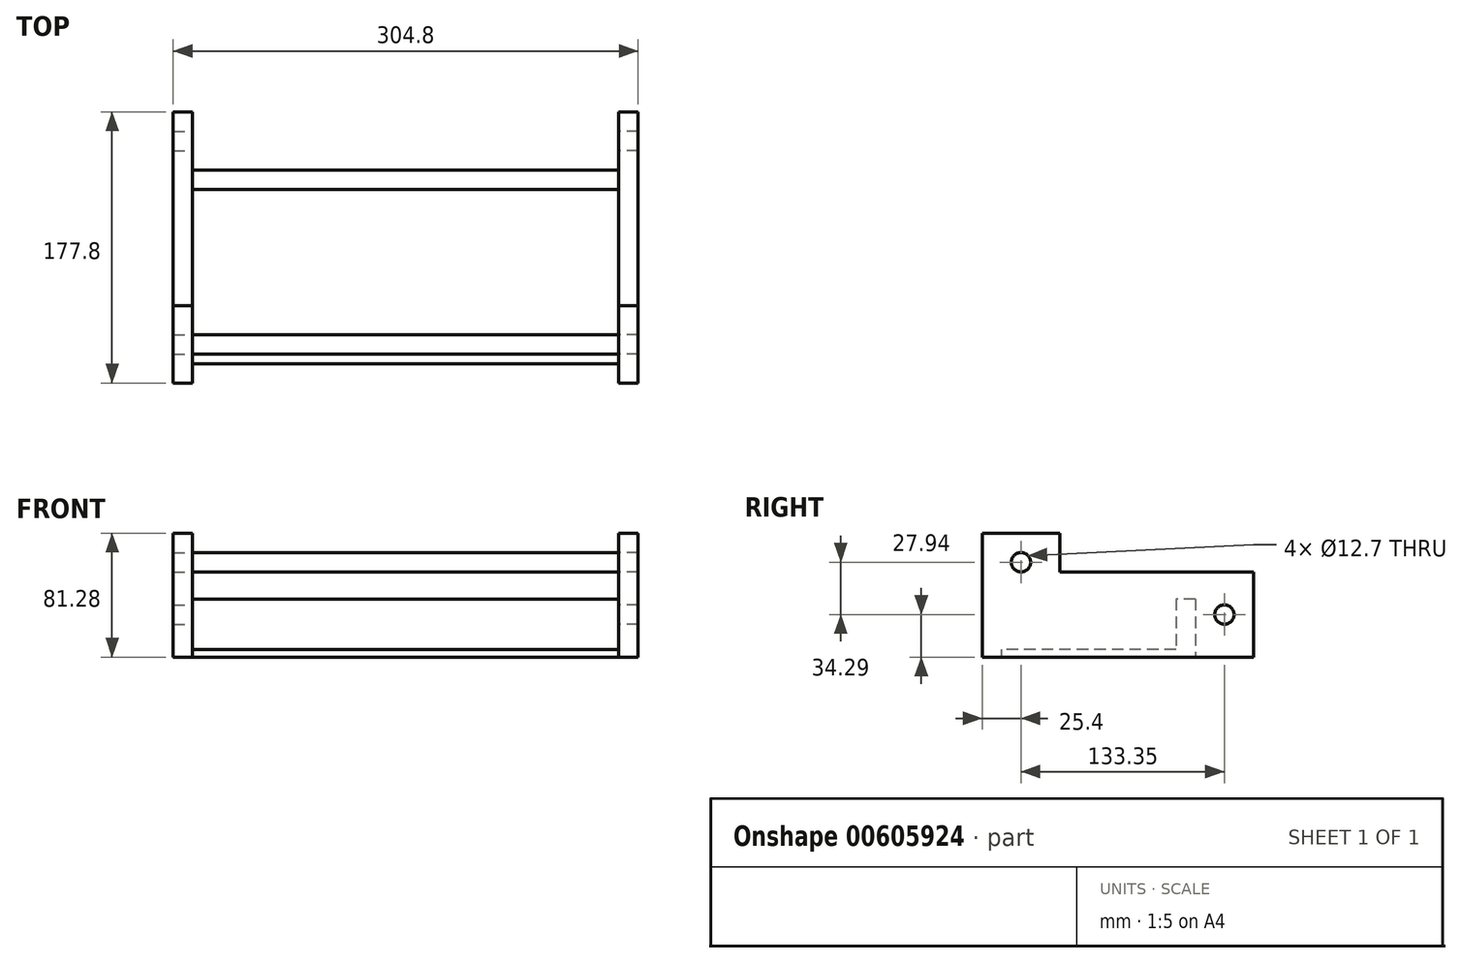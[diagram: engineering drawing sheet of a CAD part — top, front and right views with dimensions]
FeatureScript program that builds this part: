
annotation { "Feature Type Name" : "Feature", "Feature Type Description" : "" }
export const myFeature = defineFeature(function(context is Context, id is Id, definition is map)
    precondition{}
    {
        {
            var Q0;
            Q0=qCreatedBy(makeId("Top.planeOp"),FACE);
            var sketch = newSketch(context, id + "F0", { "sketchPlane" : qUnion([Q0])});
            skLineSegment(sketch, "E0.bottom", {"start": v(139.7, 63.5) * mm, "end": v(-139.7, 63.5) * mm});
            skLineSegment(sketch, "E0.top", {"start": v(139.7, -63.5) * mm, "end": v(-139.7, -63.5) * mm});
            skLineSegment(sketch, "E0.left", {"start": v(139.7, 63.5) * mm, "end": v(139.7, -63.5) * mm});
            skLineSegment(sketch, "E0.right", {"start": v(-139.7, 63.5) * mm, "end": v(-139.7, -63.5) * mm});
            skPoint(sketch, "E0.middle", {"position": v(0, 0) * mm});
            skSolve(sketch);
        }
        {
            var Q0;
            Q0 = qSketchRegion(id + "F0", true);
            extrude(context, id + "F1", {"entities" : qUnion([Q0]), "oppositeDirection" : true, "depth" : 5.08 * mm, "offsetDistance" : 25.4 * mm});
        }
        {
            var Q0;
            Q0=makeQuery(id+"F1.opExtrude","SWEPT_FACE",FACE,{"disambiguationData":[OSD([sQuery(id+"F0.wireOp",EDGE,"E0.left")])]});
            var sketch = newSketch(context, id + "F2", { "sketchPlane" : qUnion([Q0])});
            skLineSegment(sketch, "E1.bottom", {"start": v(-63.5, -5.08) * mm, "end": v(114.3, -5.08) * mm});
            skLineSegment(sketch, "E1.top", {"start": v(-63.5, 50.8) * mm, "end": v(114.3, 50.8) * mm});
            skLineSegment(sketch, "E1.left", {"start": v(-63.5, -5.08) * mm, "end": v(-63.5, 50.8) * mm});
            skLineSegment(sketch, "E1.right", {"start": v(114.3, -5.08) * mm, "end": v(114.3, 50.8) * mm});
            skLineSegment(sketch, "E2.bottom", {"start": v(-63.5, 50.8) * mm, "end": v(-12.7, 50.8) * mm});
            skLineSegment(sketch, "E2.top", {"start": v(-63.5, 76.2) * mm, "end": v(-12.7, 76.2) * mm});
            skLineSegment(sketch, "E2.left", {"start": v(-63.5, 50.8) * mm, "end": v(-63.5, 76.2) * mm});
            skLineSegment(sketch, "E2.right", {"start": v(-12.7, 50.8) * mm, "end": v(-12.7, 76.2) * mm});
            skCircle(sketch, "E3", {"center": v(-38.1, 57.15) * mm, "radius": 6.35 * mm});
            skPoint(sketch, "E3.centerSnap0", {"position": v(-38.1, 50.8) * mm});
            skCircle(sketch, "E4", {"center": v(95.25, 22.86) * mm, "radius": 6.35 * mm});
            skSolve(sketch);
        }
        {
            var Q0;
            Q0 = qSketchRegion(id + "F2", true);
            extrude(context, id + "F3", {"entities" : qUnion([Q0]), "operationType" : NewBodyOperationType.ADD, "depth" : 12.7 * mm, "offsetDistance" : 25.4 * mm});
        }
        {
            var Q0;
            Q0=makeQuery(id+"F1.opExtrude","SWEPT_BODY",BODY,{"disambiguationData":[OSD([sQuery(id+"F0.wireOp",EDGE,"E0.bottom"),sQuery(id+"F0.wireOp",EDGE,"E0.top"),sQuery(id+"F0.wireOp",EDGE,"E0.left"),sQuery(id+"F0.wireOp",EDGE,"E0.right")])]});
            var Q1;
            Q1=qCreatedBy(makeId("Right.planeOp"),FACE);
            mirror(context, id + "F4", {"operationType" : NewBodyOperationType.ADD, "entities" : qUnion([Q0]), "mirrorPlane" : qUnion([Q1])});
        }
        {
            var Q0;
            Q0=makeQuery(id+"F1.opExtrude","SWEPT_FACE",FACE,{"disambiguationData":[OSD([sQuery(id+"F0.wireOp",EDGE,"E0.bottom")])]});
            var sketch = newSketch(context, id + "F5", { "sketchPlane" : qUnion([Q0])});
            skLineSegment(sketch, "E5.bottom", {"start": v(-139.7, 33.02) * mm, "end": v(139.7, 33.02) * mm});
            skLineSegment(sketch, "E5.top", {"start": v(-139.7, -5.08) * mm, "end": v(139.7, -5.08) * mm});
            skLineSegment(sketch, "E5.left", {"start": v(-139.7, 33.02) * mm, "end": v(-139.7, -5.08) * mm});
            skLineSegment(sketch, "E5.right", {"start": v(139.7, 33.02) * mm, "end": v(139.7, -5.08) * mm});
            skSolve(sketch);
        }
        {
            var Q0;
            Q0 = qSketchRegion(id + "F5", true);
            extrude(context, id + "F6", {"entities" : qUnion([Q0]), "operationType" : NewBodyOperationType.ADD, "depth" : 12.7 * mm, "offsetDistance" : 25.4 * mm});
        }
        {
            var Q0;
            Q0=makeQuery(id+"F4.opPattern","COPY",FACE,{"derivedFrom":makeQuery(id+"F3.opExtrude","CAP_FACE",FACE,{"disambiguationData":[OSD([sQuery(id+"F2.wireOp",EDGE,"E1.bottom"),sQuery(id+"F2.wireOp",EDGE,"E1.top"),sQuery(id+"F2.wireOp",EDGE,"E1.left"),sQuery(id+"F2.wireOp",EDGE,"E1.right"),sQuery(id+"F2.wireOp",EDGE,"E2.top"),sQuery(id+"F2.wireOp",EDGE,"E2.left"),sQuery(id+"F2.wireOp",EDGE,"E2.right"),sQuery(id+"F2.wireOp",EDGE,"E4"),sQuery(id+"F2.wireOp",EDGE,"E3")])],"isStart":true}),"instanceName":"1"});
            var sketch = newSketch(context, id + "F7", { "sketchPlane" : qUnion([Q0])});
            skCircle(sketch, "E6", {"center": v(-38.1, 57.15) * mm, "radius": 6.35 * mm});
            skLineSegment(sketch, "E7", {"start": v(-38.1, 57.15) * mm, "end": v(-38.1, 0) * mm});
            skSolve(sketch);
        }
        {
            var Q0;
            Q0 = qSketchRegion(id + "F7", true);
            extrude(context, id + "F8", {"entities" : qUnion([Q0]), "depth" : 279.4 * mm, "offsetDistance" : 25.4 * mm});
        }
        {
            var Q0;
            Q0=makeQuery(id+"F1.opExtrude","CAP_FACE",FACE,{"disambiguationData":[OSD([sQuery(id+"F0.wireOp",EDGE,"E0.bottom"),sQuery(id+"F0.wireOp",EDGE,"E0.top"),sQuery(id+"F0.wireOp",EDGE,"E0.left"),sQuery(id+"F0.wireOp",EDGE,"E0.right")])],"isStart":true});
            var sketch = newSketch(context, id + "F9", { "sketchPlane" : qUnion([Q0])});
            skLineSegment(sketch, "E8.bottom", {"start": v(-139.7, -50.8) * mm, "end": v(139.7, -50.8) * mm});
            skLineSegment(sketch, "E8.top", {"start": v(-139.7, -63.5) * mm, "end": v(139.7, -63.5) * mm});
            skLineSegment(sketch, "E8.left", {"start": v(-139.7, -50.8) * mm, "end": v(-139.7, -63.5) * mm});
            skLineSegment(sketch, "E8.right", {"start": v(139.7, -50.8) * mm, "end": v(139.7, -63.5) * mm});
            skSolve(sketch);
        }
        {
            var Q0;
            Q0=makeQuery(id+"F9.imprint","IMPRINT",FACE,{"disambiguationData":[TD([[makeQuery(id+"F9.imprint","IMPRINT",EDGE,{"derivedFrom":sQuery(id+"F9.wireOp",EDGE,"E8.bottom")}),-1.0]])]});
            extrude(context, id + "F10", {"entities" : qUnion([Q0]), "operationType" : NewBodyOperationType.REMOVE, "oppositeDirection" : true, "depth" : 25.4 * mm, "offsetDistance" : 25.4 * mm});
        }
    });
